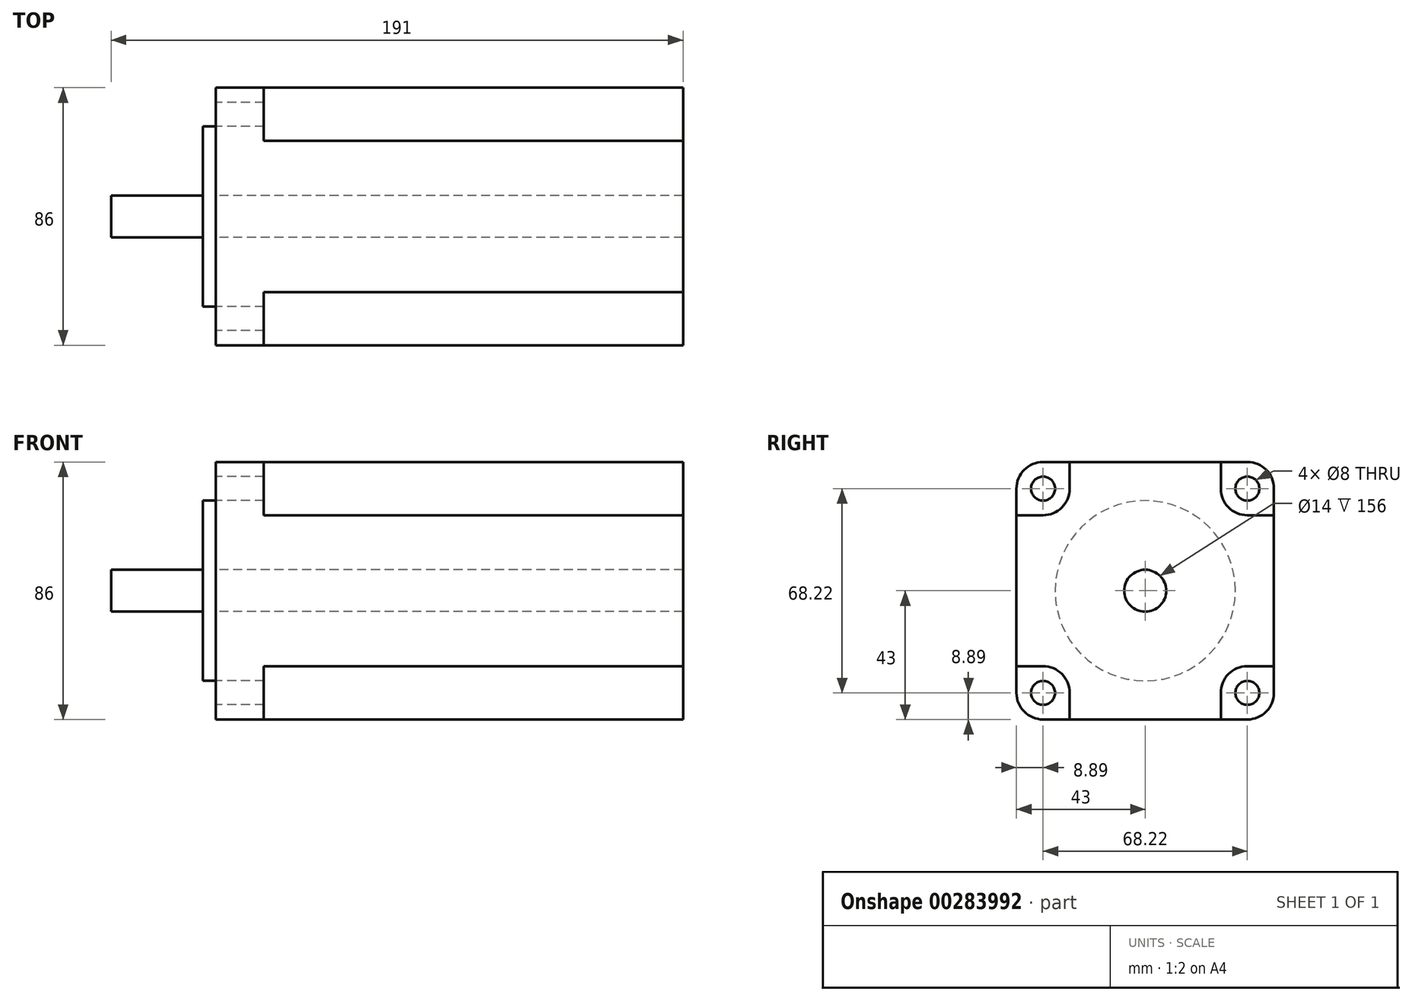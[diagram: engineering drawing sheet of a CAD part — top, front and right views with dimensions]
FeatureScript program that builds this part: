
annotation { "Feature Type Name" : "Feature", "Feature Type Description" : "" }
export const myFeature = defineFeature(function(context is Context, id is Id, definition is map)
    precondition{}
    {
        {
            var Q0;
            Q0=qCreatedBy(makeId("Right.planeOp"),FACE);
            var sketch = newSketch(context, id + "F0", { "sketchPlane" : qUnion([Q0])});
            skLineSegment(sketch, "E0.bottom", {"start": v(34.11, -43) * mm, "end": v(-34.1, -43) * mm});
            skLineSegment(sketch, "E0.top", {"start": v(34.11, 43) * mm, "end": v(-34.1, 43) * mm});
            skLineSegment(sketch, "E0.left", {"start": v(43, -34.1) * mm, "end": v(43, 34.11) * mm});
            skLineSegment(sketch, "E0.right", {"start": v(-43, -34.1) * mm, "end": v(-43, 34.1) * mm});
            skPoint(sketch, "E0.middle", {"position": v(0, 0) * mm});
            skCircle(sketch, "E1", {"center": v(0, 0) * mm, "radius": 7 * mm});
            skPoint(sketch, "E2.visualSharp", {"position": v(-43, 43) * mm});
            skArc(sketch, "E2.filletArc", {"start": v(-34.1, 43) * mm, "mid": v(-40.4, 40.4) * mm, "end": v(-43, 34.1) * mm});
            skPoint(sketch, "E3.visualSharp", {"position": v(43, 43) * mm});
            skArc(sketch, "E3.filletArc", {"start": v(43, 34.11) * mm, "mid": v(40.4, 40.4) * mm, "end": v(34.11, 43) * mm});
            skPoint(sketch, "E4.visualSharp", {"position": v(43, -43) * mm});
            skArc(sketch, "E4.filletArc", {"start": v(34.11, -43) * mm, "mid": v(40.4, -40.4) * mm, "end": v(43, -34.1) * mm});
            skPoint(sketch, "E5.visualSharp", {"position": v(-43, -43) * mm});
            skArc(sketch, "E5.filletArc", {"start": v(-43, -34.1) * mm, "mid": v(-40.4, -40.4) * mm, "end": v(-34.1, -43) * mm});
            skPoint(sketch, "E6.visualSharp", {"position": v(-52, 52) * mm});
            skPoint(sketch, "E7.visualSharp", {"position": v(52, 52) * mm});
            skPoint(sketch, "E8.visualSharp", {"position": v(52, -52) * mm});
            skPoint(sketch, "E9.visualSharp", {"position": v(-52, -52) * mm});
            skCircle(sketch, "E10", {"center": v(0, 0) * mm, "radius": 30.1 * mm});
            skLineSegment(sketch, "E11", {"start": v(-25.22, -43) * mm, "end": v(-25.22, -34.1) * mm});
            skLineSegment(sketch, "E12", {"start": v(-34.1, -25.22) * mm, "end": v(-43, -25.22) * mm});
            skLineSegment(sketch, "E13", {"start": v(-25.22, 43) * mm, "end": v(-25.22, 34.11) * mm});
            skLineSegment(sketch, "E14", {"start": v(-34.1, 25.22) * mm, "end": v(-43, 25.22) * mm});
            skLineSegment(sketch, "E15", {"start": v(25.22, 43) * mm, "end": v(25.22, 34.11) * mm});
            skLineSegment(sketch, "E16", {"start": v(34.1, 25.22) * mm, "end": v(43, 25.22) * mm});
            skLineSegment(sketch, "E17", {"start": v(25.22, -43) * mm, "end": v(25.22, -34.1) * mm});
            skLineSegment(sketch, "E18", {"start": v(34.11, -25.22) * mm, "end": v(43, -25.22) * mm});
            skPoint(sketch, "E19.visualSharp", {"position": v(-25.22, 25.22) * mm});
            skArc(sketch, "E19.filletArc", {"start": v(-34.1, 25.22) * mm, "mid": v(-27.82, 27.82) * mm, "end": v(-25.22, 34.11) * mm});
            skPoint(sketch, "E20.visualSharp", {"position": v(25.22, 25.22) * mm});
            skArc(sketch, "E20.filletArc", {"start": v(25.22, 34.11) * mm, "mid": v(27.82, 27.82) * mm, "end": v(34.1, 25.22) * mm});
            skPoint(sketch, "E21.visualSharp", {"position": v(25.22, -25.22) * mm});
            skArc(sketch, "E21.filletArc", {"start": v(34.11, -25.22) * mm, "mid": v(27.82, -27.82) * mm, "end": v(25.22, -34.1) * mm});
            skPoint(sketch, "E22.visualSharp", {"position": v(-25.22, -25.22) * mm});
            skArc(sketch, "E22.filletArc", {"start": v(-25.22, -34.1) * mm, "mid": v(-27.82, -27.82) * mm, "end": v(-34.1, -25.22) * mm});
            skCircle(sketch, "E23", {"center": v(-34.1, 34.1) * mm, "radius": 4 * mm});
            skCircle(sketch, "E24", {"center": v(34.11, 34.11) * mm, "radius": 4 * mm});
            skCircle(sketch, "E25", {"center": v(34.11, -34.1) * mm, "radius": 4 * mm});
            skCircle(sketch, "E26", {"center": v(-34.1, -34.1) * mm, "radius": 4 * mm});
            skSolve(sketch);
        }
        {
            var Q0;
            Q0=makeQuery(id+"F0.imprint","IMPRINT",FACE,{"disambiguationData":[TD([[makeQuery(id+"F0.imprint","IMPRINT",EDGE,{"derivedFrom":sQuery(id+"F0.wireOp",EDGE,"E1")}),1.0]])]});
            extrude(context, id + "F1", {"entities" : qUnion([Q0]), "oppositeDirection" : true, "depth" : 35 * mm});
        }
        {
            var Q0;
            Q0=makeQuery(id+"F0.imprint","IMPRINT",FACE,{"disambiguationData":[TD([[makeQuery(id+"F0.imprint","IMPRINT",EDGE,{"derivedFrom":sQuery(id+"F0.wireOp",EDGE,"E1")}),-1.0]])]});
            extrude(context, id + "F2", {"entities" : qUnion([Q0]), "operationType" : NewBodyOperationType.ADD, "oppositeDirection" : true, "depth" : 0.12 * 35 * mm});
        }
        {
            var Q0;
            Q0=makeQuery(id+"F0.imprint","IMPRINT",FACE,{"disambiguationData":[TD([[makeQuery(id+"F0.imprint","IMPRINT",EDGE,{"derivedFrom":sQuery(id+"F0.wireOp",EDGE,"E1")}),-1.0]])]});
            var Q1;
            Q1=makeQuery(id+"F0.imprint","IMPRINT",FACE,{"disambiguationData":[TD([[makeQuery(id+"F0.imprint","IMPRINT",EDGE,{"derivedFrom":sQuery(id+"F0.wireOp",EDGE,"E10")}),-1.0]])]});
            extrude(context, id + "F3", {"entities" : qUnion([Q0, Q1]), "operationType" : NewBodyOperationType.ADD, "depth" : 156 * mm});
        }
        {
            var Q0;
            {var subQ0=sQuery(id+"F0.wireOp",EDGE,"E2.filletArc");Q0=makeQuery(id+"F0.imprint","IMPRINT",FACE,{"disambiguationData":[TD([[makeQuery(id+"F0.imprint","IMPRINT",EDGE,{"derivedFrom":subQ0}),1.0]])]});}
            var Q1;
            {var subQ1=sQuery(id+"F0.wireOp",EDGE,"E3.filletArc");Q1=makeQuery(id+"F0.imprint","IMPRINT",FACE,{"disambiguationData":[TD([[makeQuery(id+"F0.imprint","IMPRINT",EDGE,{"derivedFrom":subQ1}),1.0]])]});}
            var Q2;
            {var subQ1=sQuery(id+"F0.wireOp",EDGE,"E4.filletArc");Q2=makeQuery(id+"F0.imprint","IMPRINT",FACE,{"disambiguationData":[TD([[makeQuery(id+"F0.imprint","IMPRINT",EDGE,{"derivedFrom":subQ1}),1.0]])]});}
            var Q3;
            {var subQ1=sQuery(id+"F0.wireOp",EDGE,"E5.filletArc");Q3=makeQuery(id+"F0.imprint","IMPRINT",FACE,{"disambiguationData":[TD([[makeQuery(id+"F0.imprint","IMPRINT",EDGE,{"derivedFrom":subQ1}),1.0]])]});}
            extrude(context, id + "F4", {"entities" : qUnion([Q0, Q1, Q2, Q3]), "operationType" : NewBodyOperationType.ADD, "depth" : 2 * 8 * mm});
        }
    });
